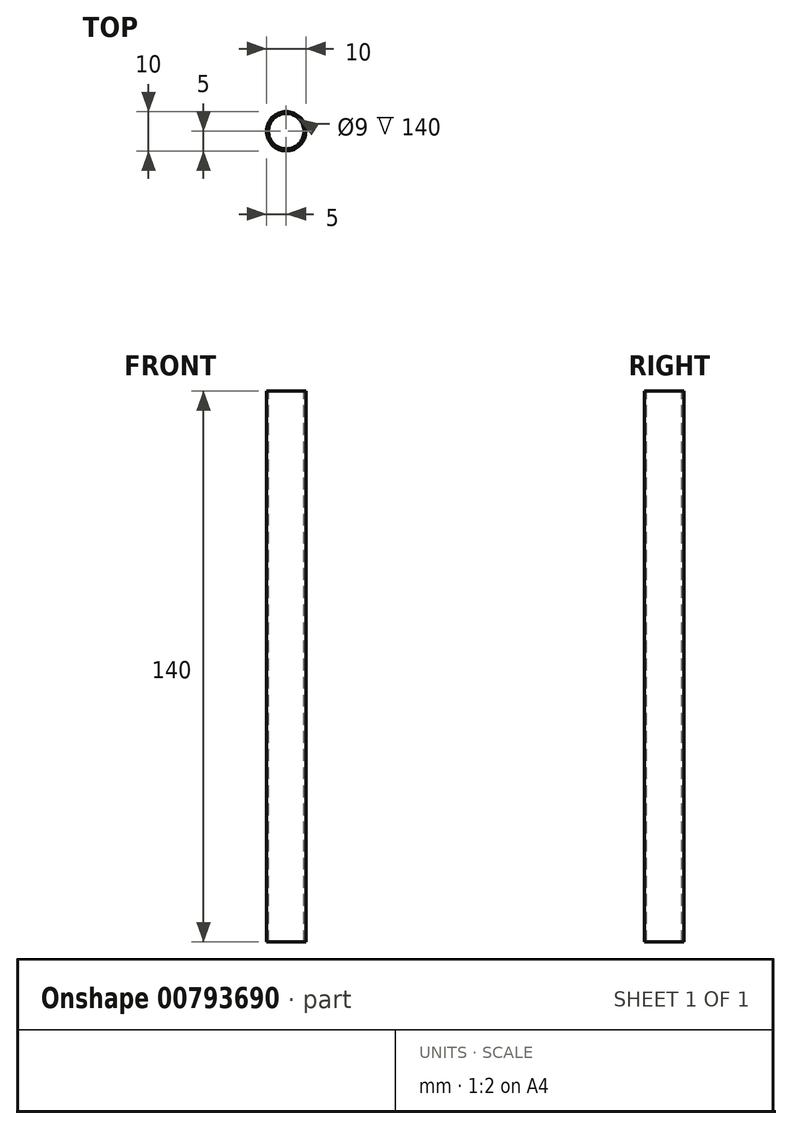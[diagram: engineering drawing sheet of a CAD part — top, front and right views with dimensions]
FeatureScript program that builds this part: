
annotation { "Feature Type Name" : "Feature", "Feature Type Description" : "" }
export const myFeature = defineFeature(function(context is Context, id is Id, definition is map)
    precondition{}
    {
        {
            var Q0;
            Q0=qCreatedBy(makeId("Top.planeOp"),FACE);
            var sketch = newSketch(context, id + "F0", { "sketchPlane" : qUnion([Q0])});
            skCircle(sketch, "E0", {"center": v(0, 0) * mm, "radius": 4.5 * mm});
            skCircle(sketch, "E1", {"center": v(0, 0) * mm, "radius": 5 * mm});
            skSolve(sketch);
        }
        {
            var Q0;
            Q0=makeQuery(id+"F0.imprint","IMPRINT",FACE,{"disambiguationData":[TD([[makeQuery(id+"F0.imprint","IMPRINT",EDGE,{"derivedFrom":sQuery(id+"F0.wireOp",EDGE,"E0")}),-1.0]])]});
            extrude(context, id + "F1", {"entities" : qUnion([Q0]), "oppositeDirection" : true, "depth" : 140 * mm, "offsetDistance" : 25 * mm});
        }
    });
